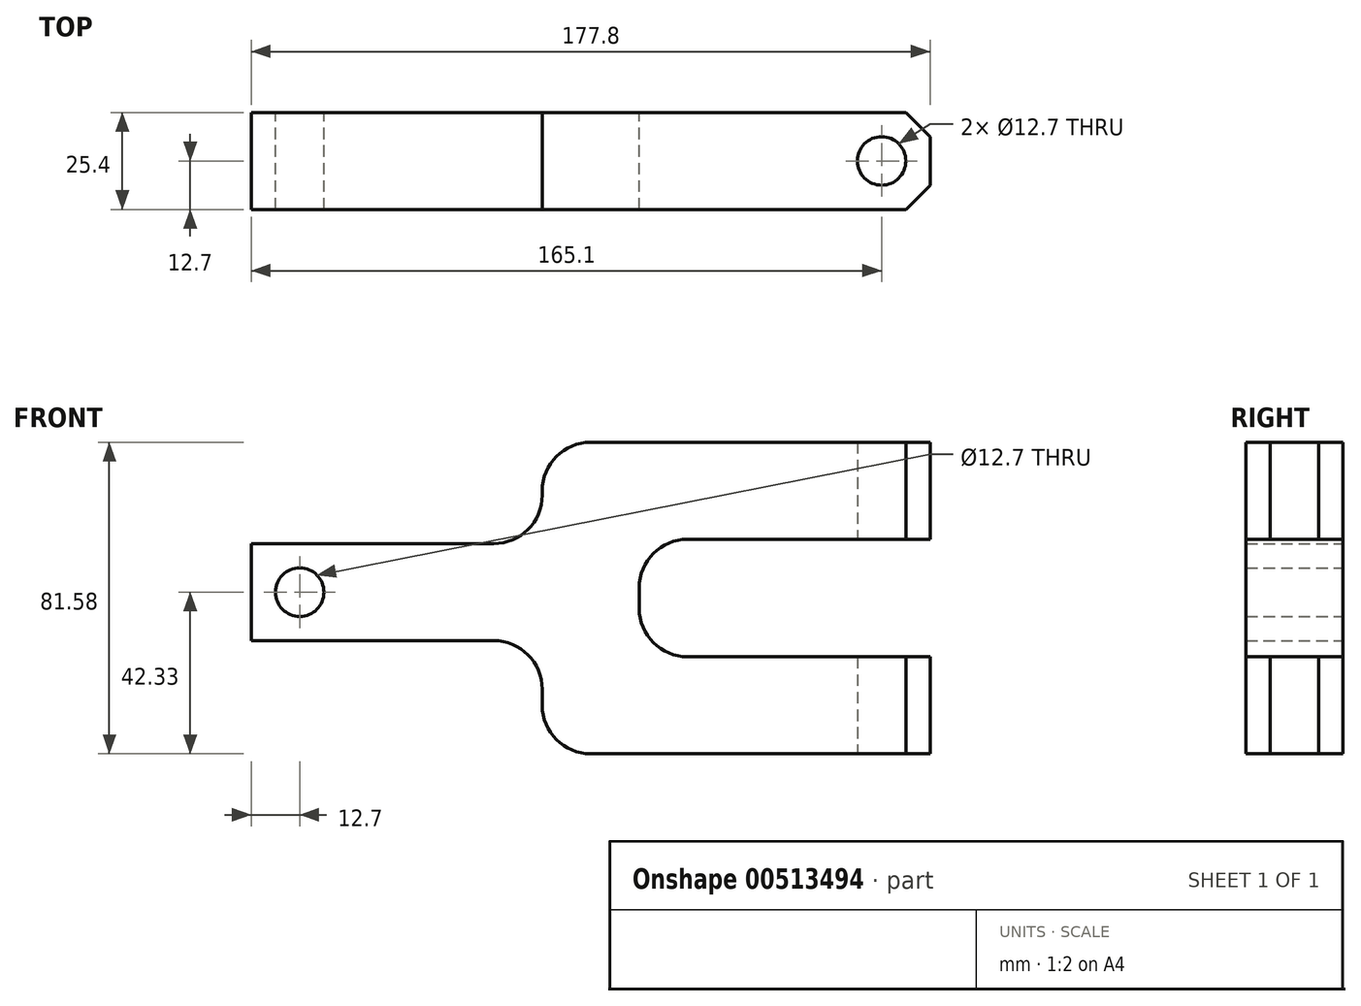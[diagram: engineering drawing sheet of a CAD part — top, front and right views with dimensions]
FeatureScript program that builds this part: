
annotation { "Feature Type Name" : "Feature", "Feature Type Description" : "" }
export const myFeature = defineFeature(function(context is Context, id is Id, definition is map)
    precondition{}
    {
        {
            var Q0;
            Q0=qCreatedBy(makeId("Front.planeOp"),FACE);
            var sketch = newSketch(context, id + "F0", { "sketchPlane" : qUnion([Q0])});
            skLineSegment(sketch, "E0.bottom", {"start": v(-63.5, -12.7) * mm, "end": v(-127, -12.7) * mm});
            skLineSegment(sketch, "E0.top", {"start": v(-63.5, 12.7) * mm, "end": v(-127, 12.7) * mm});
            skLineSegment(sketch, "E0.left", {"start": v(-25.4, -4.23) * mm, "end": v(-25.4, 1.15) * mm});
            skLineSegment(sketch, "E0.right", {"start": v(-127, -12.7) * mm, "end": v(-127, 12.7) * mm});
            skPoint(sketch, "E0.middle", {"position": v(-76.2, 0) * mm});
            skLineSegment(sketch, "E1.bottom", {"start": v(-38.1, 39.25) * mm, "end": v(50.8, 39.25) * mm});
            skLineSegment(sketch, "E1.top", {"start": v(-12.7, 13.85) * mm, "end": v(50.8, 13.85) * mm});
            skLineSegment(sketch, "E1.left", {"start": v(-50.8, 26.55) * mm, "end": v(-50.8, 25.4) * mm});
            skLineSegment(sketch, "E1.right", {"start": v(50.8, 39.25) * mm, "end": v(50.8, 13.85) * mm});
            skPoint(sketch, "E1.middle", {"position": v(0, 26.55) * mm});
            skLineSegment(sketch, "E2.bottom", {"start": v(50.8, -42.33) * mm, "end": v(-38.1, -42.33) * mm});
            skLineSegment(sketch, "E2.top", {"start": v(50.8, -16.93) * mm, "end": v(-12.7, -16.93) * mm});
            skLineSegment(sketch, "E2.left", {"start": v(50.8, -42.33) * mm, "end": v(50.8, -16.93) * mm});
            skLineSegment(sketch, "E2.right", {"start": v(-50.8, -29.63) * mm, "end": v(-50.8, -25.4) * mm});
            skPoint(sketch, "E2.middle", {"position": v(0, -29.63) * mm});
            skPoint(sketch, "E3.visualSharp", {"position": v(-50.8, 39.25) * mm});
            skArc(sketch, "E3.filletArc", {"start": v(-38.1, 39.25) * mm, "mid": v(-47.08, 35.53) * mm, "end": v(-50.8, 26.55) * mm});
            skPoint(sketch, "E4.newPointA", {"position": v(-50.8, 13.85) * mm});
            skPoint(sketch, "E4.newPointB", {"position": v(-25.4, 12.7) * mm});
            skArc(sketch, "E4.filletArc", {"start": v(-63.5, 12.7) * mm, "mid": v(-54.52, 16.42) * mm, "end": v(-50.8, 25.4) * mm});
            skPoint(sketch, "E5.newPointB", {"position": v(-25.4, -12.7) * mm});
            skArc(sketch, "E5.filletArc", {"start": v(-50.8, -25.4) * mm, "mid": v(-54.52, -16.42) * mm, "end": v(-63.5, -12.7) * mm});
            skPoint(sketch, "E6.newPointB", {"position": v(-50.8, -16.93) * mm});
            skArc(sketch, "E6.filletArc", {"start": v(-25.4, -4.23) * mm, "mid": v(-21.68, -13.21) * mm, "end": v(-12.7, -16.93) * mm});
            skArc(sketch, "E7.filletArc", {"start": v(-12.7, 13.85) * mm, "mid": v(-21.68, 10.13) * mm, "end": v(-25.4, 1.15) * mm});
            skCircle(sketch, "E8", {"center": v(-114.3, 0) * mm, "radius": 6.35 * mm});
            skPoint(sketch, "E9.visualSharp", {"position": v(-50.8, -42.33) * mm});
            skArc(sketch, "E9.filletArc", {"start": v(-50.8, -29.63) * mm, "mid": v(-47.08, -38.61) * mm, "end": v(-38.1, -42.33) * mm});
            skSolve(sketch);
        }
        {
            var Q0;
            Q0 = qSketchRegion(id + "F0", true);
            var Q1;
            Q1 = qSketchRegion(id + "F2", true);
            extrude(context, id + "F1", {"entities" : qUnion([Q0, Q1]), "endBound" : BoundingType.SYMMETRIC, "depth" : 25.4 * mm, "offsetDistance" : 25.4 * mm});
        }
        {
            var Q0;
            Q0=makeQuery(id+"F1.opExtrude","SWEPT_FACE",FACE,{"disambiguationData":[OSD([sQuery(id+"F0.wireOp",EDGE,"E1.top")])]});
            var sketch = newSketch(context, id + "F2", { "sketchPlane" : qUnion([Q0])});
            skCircle(sketch, "E10", {"center": v(38.1, 0) * mm, "radius": 6.35 * mm});
            skSolve(sketch);
        }
        {
            var Q0;
            Q0 = qSketchRegion(id + "F2", true);
            extrude(context, id + "F3", {"entities" : qUnion([Q0]), "operationType" : NewBodyOperationType.REMOVE, "oppositeDirection" : true, "depth" : 25.4 * mm, "offsetDistance" : 25.4 * mm});
        }
        {
            var Q0;
            Q0=makeQuery(id+"F1.opExtrude","SWEPT_FACE",FACE,{"disambiguationData":[OSD([sQuery(id+"F0.wireOp",EDGE,"E2.bottom")])]});
            var sketch = newSketch(context, id + "F4", { "sketchPlane" : qUnion([Q0])});
            skCircle(sketch, "E11", {"center": v(38.1, 0) * mm, "radius": 6.35 * mm});
            skSolve(sketch);
        }
        {
            var Q0;
            Q0 = qSketchRegion(id + "F4", true);
            extrude(context, id + "F5", {"entities" : qUnion([Q0]), "operationType" : NewBodyOperationType.REMOVE, "oppositeDirection" : true, "depth" : 25.4 * mm, "offsetDistance" : 25.4 * mm});
        }
        {
            var Q0;
            Q0=makeQuery(id+"F1.opExtrude","CAP_EDGE",EDGE,{"disambiguationData":[OSD([sQuery(id+"F0.wireOp",EDGE,"E2.left")])],"isStart":false});
            var Q1;
            Q1=makeQuery(id+"F1.opExtrude","CAP_EDGE",EDGE,{"disambiguationData":[OSD([sQuery(id+"F0.wireOp",EDGE,"E2.left")])],"isStart":true});
            var Q2;
            Q2=makeQuery(id+"F1.opExtrude","CAP_EDGE",EDGE,{"disambiguationData":[OSD([sQuery(id+"F0.wireOp",EDGE,"E1.right")])],"isStart":false});
            var Q3;
            Q3=makeQuery(id+"F1.opExtrude","CAP_EDGE",EDGE,{"disambiguationData":[OSD([sQuery(id+"F0.wireOp",EDGE,"E1.right")])],"isStart":true});
            chamfer(context, id + "F6", {"entities" : qUnion([Q0, Q1, Q2, Q3]), "width" : 6.35 * mm, "tangentPropagation" : true});
        }
    });
